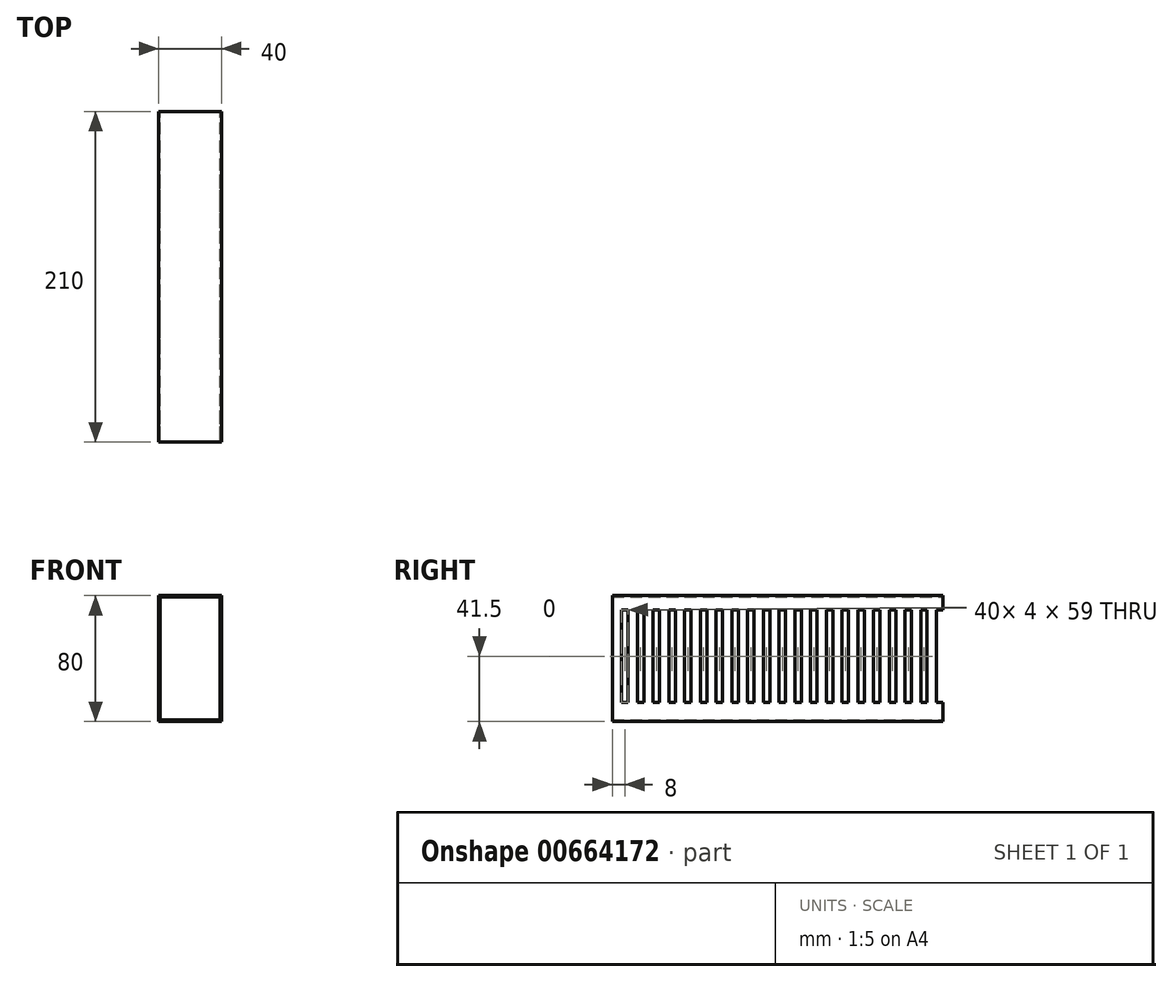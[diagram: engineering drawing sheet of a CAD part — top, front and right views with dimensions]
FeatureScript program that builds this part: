
annotation { "Feature Type Name" : "Feature", "Feature Type Description" : "" }
export const myFeature = defineFeature(function(context is Context, id is Id, definition is map)
    precondition{}
    {
        {
            assignVariable(context, id + "F0", {"name" : "TrunkingLength", "anyValue" : 210});
        }
        {
            var Q0;
            Q0=qCreatedBy(makeId("Front.planeOp"),FACE);
            var sketch = newSketch(context, id + "F1", { "sketchPlane" : qUnion([Q0])});
            skLineSegment(sketch, "E0.bottom", {"start": v(-20, 40) * mm, "end": v(20, 40) * mm});
            skLineSegment(sketch, "E0.top", {"start": v(-20, -40) * mm, "end": v(20, -40) * mm});
            skLineSegment(sketch, "E0.left", {"start": v(-20, 40) * mm, "end": v(-20, -40) * mm});
            skLineSegment(sketch, "E0.right", {"start": v(20, 40) * mm, "end": v(20, -40) * mm});
            skSolve(sketch);
        }
        {
            var Q0;
            Q0=makeQuery(id+"F1.imprint","IMPRINT",FACE,{"disambiguationData":[TD([[makeQuery(id+"F1.imprint","IMPRINT",EDGE,{"derivedFrom":sQuery(id+"F1.wireOp",EDGE,"E0.bottom")}),-1.0]])]});
            extrude(context, id + "F2", {"entities" : qUnion([Q0]), "depth" : (getVariable(context, 'TrunkingLength')) * mm});
        }
        {
            var Q0;
            Q0=makeQuery(id+"F2.opExtrude","CAP_FACE",FACE,{"disambiguationData":[OSD([sQuery(id+"F1.wireOp",EDGE,"E0.bottom"),sQuery(id+"F1.wireOp",EDGE,"E0.top"),sQuery(id+"F1.wireOp",EDGE,"E0.left"),sQuery(id+"F1.wireOp",EDGE,"E0.right")])],"isStart":false});
            var Q1;
            Q1=makeQuery(id+"F2.opExtrude","CAP_FACE",FACE,{"disambiguationData":[OSD([sQuery(id+"F1.wireOp",EDGE,"E0.bottom"),sQuery(id+"F1.wireOp",EDGE,"E0.top"),sQuery(id+"F1.wireOp",EDGE,"E0.left"),sQuery(id+"F1.wireOp",EDGE,"E0.right")])],"isStart":true});
            shell(context, id + "F3", {"entities" : qUnion([Q0, Q1]), "thickness" : 1 * mm});
        }
        {
            var Q0;
            Q0=makeQuery(id+"F2.opExtrude","SWEPT_FACE",FACE,{"disambiguationData":[OSD([sQuery(id+"F1.wireOp",EDGE,"E0.right")])]});
            var sketch = newSketch(context, id + "F4", { "sketchPlane" : qUnion([Q0])});
            skLineSegment(sketch, "E1.bottom", {"start": v(-204, 31) * mm, "end": v(-200, 31) * mm});
            skLineSegment(sketch, "E1.top", {"start": v(-204, -28) * mm, "end": v(-200, -28) * mm});
            skLineSegment(sketch, "E1.left", {"start": v(-204, 31) * mm, "end": v(-204, -28) * mm});
            skLineSegment(sketch, "E1.right", {"start": v(-200, 31) * mm, "end": v(-200, -28) * mm});
            skLineSegment(sketch, "E2.1.0.0", {"start": v(-194, 31) * mm, "end": v(-194, -28) * mm});
            skLineSegment(sketch, "E2.1.0.1", {"start": v(-190, 31) * mm, "end": v(-190, -28) * mm});
            skLineSegment(sketch, "E2.1.0.2", {"start": v(-194, 31) * mm, "end": v(-190, 31) * mm});
            skLineSegment(sketch, "E2.1.0.3", {"start": v(-194, -28) * mm, "end": v(-190, -28) * mm});
            skLineSegment(sketch, "E2.2.0.0", {"start": v(-184, 31) * mm, "end": v(-184, -28) * mm});
            skLineSegment(sketch, "E2.2.0.1", {"start": v(-180, 31) * mm, "end": v(-180, -28) * mm});
            skLineSegment(sketch, "E2.2.0.2", {"start": v(-184, 31) * mm, "end": v(-180, 31) * mm});
            skLineSegment(sketch, "E2.2.0.3", {"start": v(-184, -28) * mm, "end": v(-180, -28) * mm});
            skLineSegment(sketch, "E2.3.0.0", {"start": v(-174, 31) * mm, "end": v(-174, -28) * mm});
            skLineSegment(sketch, "E2.3.0.1", {"start": v(-170, 31) * mm, "end": v(-170, -28) * mm});
            skLineSegment(sketch, "E2.3.0.2", {"start": v(-174, 31) * mm, "end": v(-170, 31) * mm});
            skLineSegment(sketch, "E2.3.0.3", {"start": v(-174, -28) * mm, "end": v(-170, -28) * mm});
            skLineSegment(sketch, "E2.4.0.0", {"start": v(-164, 31) * mm, "end": v(-164, -28) * mm});
            skLineSegment(sketch, "E2.4.0.1", {"start": v(-160, 31) * mm, "end": v(-160, -28) * mm});
            skLineSegment(sketch, "E2.4.0.2", {"start": v(-164, 31) * mm, "end": v(-160, 31) * mm});
            skLineSegment(sketch, "E2.4.0.3", {"start": v(-164, -28) * mm, "end": v(-160, -28) * mm});
            skLineSegment(sketch, "E2.5.0.0", {"start": v(-154, 31) * mm, "end": v(-154, -28) * mm});
            skLineSegment(sketch, "E2.5.0.1", {"start": v(-150, 31) * mm, "end": v(-150, -28) * mm});
            skLineSegment(sketch, "E2.5.0.2", {"start": v(-154, 31) * mm, "end": v(-150, 31) * mm});
            skLineSegment(sketch, "E2.5.0.3", {"start": v(-154, -28) * mm, "end": v(-150, -28) * mm});
            skLineSegment(sketch, "E2.6.0.0", {"start": v(-144, 31) * mm, "end": v(-144, -28) * mm});
            skLineSegment(sketch, "E2.6.0.1", {"start": v(-140, 31) * mm, "end": v(-140, -28) * mm});
            skLineSegment(sketch, "E2.6.0.2", {"start": v(-144, 31) * mm, "end": v(-140, 31) * mm});
            skLineSegment(sketch, "E2.6.0.3", {"start": v(-144, -28) * mm, "end": v(-140, -28) * mm});
            skLineSegment(sketch, "E2.7.0.0", {"start": v(-134, 31) * mm, "end": v(-134, -28) * mm});
            skLineSegment(sketch, "E2.7.0.1", {"start": v(-130, 31) * mm, "end": v(-130, -28) * mm});
            skLineSegment(sketch, "E2.7.0.2", {"start": v(-134, 31) * mm, "end": v(-130, 31) * mm});
            skLineSegment(sketch, "E2.7.0.3", {"start": v(-134, -28) * mm, "end": v(-130, -28) * mm});
            skLineSegment(sketch, "E2.8.0.0", {"start": v(-124, 31) * mm, "end": v(-124, -28) * mm});
            skLineSegment(sketch, "E2.8.0.1", {"start": v(-120, 31) * mm, "end": v(-120, -28) * mm});
            skLineSegment(sketch, "E2.8.0.2", {"start": v(-124, 31) * mm, "end": v(-120, 31) * mm});
            skLineSegment(sketch, "E2.8.0.3", {"start": v(-124, -28) * mm, "end": v(-120, -28) * mm});
            skLineSegment(sketch, "E2.9.0.0", {"start": v(-114, 31) * mm, "end": v(-114, -28) * mm});
            skLineSegment(sketch, "E2.9.0.1", {"start": v(-110, 31) * mm, "end": v(-110, -28) * mm});
            skLineSegment(sketch, "E2.9.0.2", {"start": v(-114, 31) * mm, "end": v(-110, 31) * mm});
            skLineSegment(sketch, "E2.9.0.3", {"start": v(-114, -28) * mm, "end": v(-110, -28) * mm});
            skLineSegment(sketch, "E2.10.0.0", {"start": v(-104, 31) * mm, "end": v(-104, -28) * mm});
            skLineSegment(sketch, "E2.10.0.1", {"start": v(-100, 31) * mm, "end": v(-100, -28) * mm});
            skLineSegment(sketch, "E2.10.0.2", {"start": v(-104, 31) * mm, "end": v(-100, 31) * mm});
            skLineSegment(sketch, "E2.10.0.3", {"start": v(-104, -28) * mm, "end": v(-100, -28) * mm});
            skLineSegment(sketch, "E2.11.0.0", {"start": v(-94, 31) * mm, "end": v(-94, -28) * mm});
            skLineSegment(sketch, "E2.11.0.1", {"start": v(-90, 31) * mm, "end": v(-90, -28) * mm});
            skLineSegment(sketch, "E2.11.0.2", {"start": v(-94, 31) * mm, "end": v(-90, 31) * mm});
            skLineSegment(sketch, "E2.11.0.3", {"start": v(-94, -28) * mm, "end": v(-90, -28) * mm});
            skLineSegment(sketch, "E2.12.0.0", {"start": v(-84, 31) * mm, "end": v(-84, -28) * mm});
            skLineSegment(sketch, "E2.12.0.1", {"start": v(-80, 31) * mm, "end": v(-80, -28) * mm});
            skLineSegment(sketch, "E2.12.0.2", {"start": v(-84, 31) * mm, "end": v(-80, 31) * mm});
            skLineSegment(sketch, "E2.12.0.3", {"start": v(-84, -28) * mm, "end": v(-80, -28) * mm});
            skLineSegment(sketch, "E2.13.0.0", {"start": v(-74, 31) * mm, "end": v(-74, -28) * mm});
            skLineSegment(sketch, "E2.13.0.1", {"start": v(-70, 31) * mm, "end": v(-70, -28) * mm});
            skLineSegment(sketch, "E2.13.0.2", {"start": v(-74, 31) * mm, "end": v(-70, 31) * mm});
            skLineSegment(sketch, "E2.13.0.3", {"start": v(-74, -28) * mm, "end": v(-70, -28) * mm});
            skLineSegment(sketch, "E2.14.0.0", {"start": v(-64, 31) * mm, "end": v(-64, -28) * mm});
            skLineSegment(sketch, "E2.14.0.1", {"start": v(-60, 31) * mm, "end": v(-60, -28) * mm});
            skLineSegment(sketch, "E2.14.0.2", {"start": v(-64, 31) * mm, "end": v(-60, 31) * mm});
            skLineSegment(sketch, "E2.14.0.3", {"start": v(-64, -28) * mm, "end": v(-60, -28) * mm});
            skLineSegment(sketch, "E2.15.0.0", {"start": v(-54, 31) * mm, "end": v(-54, -28) * mm});
            skLineSegment(sketch, "E2.15.0.1", {"start": v(-50, 31) * mm, "end": v(-50, -28) * mm});
            skLineSegment(sketch, "E2.15.0.2", {"start": v(-54, 31) * mm, "end": v(-50, 31) * mm});
            skLineSegment(sketch, "E2.15.0.3", {"start": v(-54, -28) * mm, "end": v(-50, -28) * mm});
            skLineSegment(sketch, "E2.16.0.0", {"start": v(-44, 31) * mm, "end": v(-44, -28) * mm});
            skLineSegment(sketch, "E2.16.0.1", {"start": v(-40, 31) * mm, "end": v(-40, -28) * mm});
            skLineSegment(sketch, "E2.16.0.2", {"start": v(-44, 31) * mm, "end": v(-40, 31) * mm});
            skLineSegment(sketch, "E2.16.0.3", {"start": v(-44, -28) * mm, "end": v(-40, -28) * mm});
            skLineSegment(sketch, "E2.17.0.0", {"start": v(-34, 31) * mm, "end": v(-34, -28) * mm});
            skLineSegment(sketch, "E2.17.0.1", {"start": v(-30, 31) * mm, "end": v(-30, -28) * mm});
            skLineSegment(sketch, "E2.17.0.2", {"start": v(-34, 31) * mm, "end": v(-30, 31) * mm});
            skLineSegment(sketch, "E2.17.0.3", {"start": v(-34, -28) * mm, "end": v(-30, -28) * mm});
            skLineSegment(sketch, "E2.18.0.0", {"start": v(-24, 31) * mm, "end": v(-24, -28) * mm});
            skLineSegment(sketch, "E2.18.0.1", {"start": v(-20, 31) * mm, "end": v(-20, -28) * mm});
            skLineSegment(sketch, "E2.18.0.2", {"start": v(-24, 31) * mm, "end": v(-20, 31) * mm});
            skLineSegment(sketch, "E2.18.0.3", {"start": v(-24, -28) * mm, "end": v(-20, -28) * mm});
            skLineSegment(sketch, "E2.19.0.0", {"start": v(-14, 31) * mm, "end": v(-14, -28) * mm});
            skLineSegment(sketch, "E2.19.0.1", {"start": v(-10, 31) * mm, "end": v(-10, -28) * mm});
            skLineSegment(sketch, "E2.19.0.2", {"start": v(-14, 31) * mm, "end": v(-10, 31) * mm});
            skLineSegment(sketch, "E2.19.0.3", {"start": v(-14, -28) * mm, "end": v(-10, -28) * mm});
            skLineSegment(sketch, "E2.20.0.0", {"start": v(-4, 31) * mm, "end": v(-4, -28) * mm});
            skLineSegment(sketch, "E2.20.0.1", {"start": v(0, 31) * mm, "end": v(0, -28) * mm});
            skLineSegment(sketch, "E2.20.0.2", {"start": v(-4, 31) * mm, "end": v(0, 31) * mm});
            skLineSegment(sketch, "E2.20.0.3", {"start": v(-4, -28) * mm, "end": v(0, -28) * mm});
            skLineSegment(sketch, "E2.21.0.0", {"start": v(6, 31) * mm, "end": v(6, -28) * mm});
            skLineSegment(sketch, "E2.21.0.1", {"start": v(10, 31) * mm, "end": v(10, -28) * mm});
            skLineSegment(sketch, "E2.21.0.2", {"start": v(6, 31) * mm, "end": v(10, 31) * mm});
            skLineSegment(sketch, "E2.21.0.3", {"start": v(6, -28) * mm, "end": v(10, -28) * mm});
            skLineSegment(sketch, "E2.22.0.0", {"start": v(16, 31) * mm, "end": v(16, -28) * mm});
            skLineSegment(sketch, "E2.22.0.1", {"start": v(20, 31) * mm, "end": v(20, -28) * mm});
            skLineSegment(sketch, "E2.22.0.2", {"start": v(16, 31) * mm, "end": v(20, 31) * mm});
            skLineSegment(sketch, "E2.22.0.3", {"start": v(16, -28) * mm, "end": v(20, -28) * mm});
            skLineSegment(sketch, "E2.23.0.0", {"start": v(26, 31) * mm, "end": v(26, -28) * mm});
            skLineSegment(sketch, "E2.23.0.1", {"start": v(30, 31) * mm, "end": v(30, -28) * mm});
            skLineSegment(sketch, "E2.23.0.2", {"start": v(26, 31) * mm, "end": v(30, 31) * mm});
            skLineSegment(sketch, "E2.23.0.3", {"start": v(26, -28) * mm, "end": v(30, -28) * mm});
            skLineSegment(sketch, "E2.24.0.0", {"start": v(36, 31) * mm, "end": v(36, -28) * mm});
            skLineSegment(sketch, "E2.24.0.1", {"start": v(40, 31) * mm, "end": v(40, -28) * mm});
            skLineSegment(sketch, "E2.24.0.2", {"start": v(36, 31) * mm, "end": v(40, 31) * mm});
            skLineSegment(sketch, "E2.24.0.3", {"start": v(36, -28) * mm, "end": v(40, -28) * mm});
            skLineSegment(sketch, "E2.25.0.0", {"start": v(46, 31) * mm, "end": v(46, -28) * mm});
            skLineSegment(sketch, "E2.25.0.1", {"start": v(50, 31) * mm, "end": v(50, -28) * mm});
            skLineSegment(sketch, "E2.25.0.2", {"start": v(46, 31) * mm, "end": v(50, 31) * mm});
            skLineSegment(sketch, "E2.25.0.3", {"start": v(46, -28) * mm, "end": v(50, -28) * mm});
            skLineSegment(sketch, "E2.26.0.0", {"start": v(56, 31) * mm, "end": v(56, -28) * mm});
            skLineSegment(sketch, "E2.26.0.1", {"start": v(60, 31) * mm, "end": v(60, -28) * mm});
            skLineSegment(sketch, "E2.26.0.2", {"start": v(56, 31) * mm, "end": v(60, 31) * mm});
            skLineSegment(sketch, "E2.26.0.3", {"start": v(56, -28) * mm, "end": v(60, -28) * mm});
            skLineSegment(sketch, "E2.27.0.0", {"start": v(66, 31) * mm, "end": v(66, -28) * mm});
            skLineSegment(sketch, "E2.27.0.1", {"start": v(70, 31) * mm, "end": v(70, -28) * mm});
            skLineSegment(sketch, "E2.27.0.2", {"start": v(66, 31) * mm, "end": v(70, 31) * mm});
            skLineSegment(sketch, "E2.27.0.3", {"start": v(66, -28) * mm, "end": v(70, -28) * mm});
            skLineSegment(sketch, "E2.28.0.0", {"start": v(76, 31) * mm, "end": v(76, -28) * mm});
            skLineSegment(sketch, "E2.28.0.1", {"start": v(80, 31) * mm, "end": v(80, -28) * mm});
            skLineSegment(sketch, "E2.28.0.2", {"start": v(76, 31) * mm, "end": v(80, 31) * mm});
            skLineSegment(sketch, "E2.28.0.3", {"start": v(76, -28) * mm, "end": v(80, -28) * mm});
            skLineSegment(sketch, "E2.29.0.0", {"start": v(86, 31) * mm, "end": v(86, -28) * mm});
            skLineSegment(sketch, "E2.29.0.1", {"start": v(90, 31) * mm, "end": v(90, -28) * mm});
            skLineSegment(sketch, "E2.29.0.2", {"start": v(86, 31) * mm, "end": v(90, 31) * mm});
            skLineSegment(sketch, "E2.29.0.3", {"start": v(86, -28) * mm, "end": v(90, -28) * mm});
            skLineSegment(sketch, "E2.30.0.0", {"start": v(96, 31) * mm, "end": v(96, -28) * mm});
            skLineSegment(sketch, "E2.30.0.1", {"start": v(100, 31) * mm, "end": v(100, -28) * mm});
            skLineSegment(sketch, "E2.30.0.2", {"start": v(96, 31) * mm, "end": v(100, 31) * mm});
            skLineSegment(sketch, "E2.30.0.3", {"start": v(96, -28) * mm, "end": v(100, -28) * mm});
            skLineSegment(sketch, "E2.31.0.0", {"start": v(106, 31) * mm, "end": v(106, -28) * mm});
            skLineSegment(sketch, "E2.31.0.1", {"start": v(110, 31) * mm, "end": v(110, -28) * mm});
            skLineSegment(sketch, "E2.31.0.2", {"start": v(106, 31) * mm, "end": v(110, 31) * mm});
            skLineSegment(sketch, "E2.31.0.3", {"start": v(106, -28) * mm, "end": v(110, -28) * mm});
            skLineSegment(sketch, "E2.32.0.0", {"start": v(116, 31) * mm, "end": v(116, -28) * mm});
            skLineSegment(sketch, "E2.32.0.1", {"start": v(120, 31) * mm, "end": v(120, -28) * mm});
            skLineSegment(sketch, "E2.32.0.2", {"start": v(116, 31) * mm, "end": v(120, 31) * mm});
            skLineSegment(sketch, "E2.32.0.3", {"start": v(116, -28) * mm, "end": v(120, -28) * mm});
            skLineSegment(sketch, "E2.33.0.0", {"start": v(126, 31) * mm, "end": v(126, -28) * mm});
            skLineSegment(sketch, "E2.33.0.1", {"start": v(130, 31) * mm, "end": v(130, -28) * mm});
            skLineSegment(sketch, "E2.33.0.2", {"start": v(126, 31) * mm, "end": v(130, 31) * mm});
            skLineSegment(sketch, "E2.33.0.3", {"start": v(126, -28) * mm, "end": v(130, -28) * mm});
            skLineSegment(sketch, "E2.34.0.0", {"start": v(136, 31) * mm, "end": v(136, -28) * mm});
            skLineSegment(sketch, "E2.34.0.1", {"start": v(140, 31) * mm, "end": v(140, -28) * mm});
            skLineSegment(sketch, "E2.34.0.2", {"start": v(136, 31) * mm, "end": v(140, 31) * mm});
            skLineSegment(sketch, "E2.34.0.3", {"start": v(136, -28) * mm, "end": v(140, -28) * mm});
            skLineSegment(sketch, "E2.35.0.0", {"start": v(146, 31) * mm, "end": v(146, -28) * mm});
            skLineSegment(sketch, "E2.35.0.1", {"start": v(150, 31) * mm, "end": v(150, -28) * mm});
            skLineSegment(sketch, "E2.35.0.2", {"start": v(146, 31) * mm, "end": v(150, 31) * mm});
            skLineSegment(sketch, "E2.35.0.3", {"start": v(146, -28) * mm, "end": v(150, -28) * mm});
            skLineSegment(sketch, "E2.36.0.0", {"start": v(156, 31) * mm, "end": v(156, -28) * mm});
            skLineSegment(sketch, "E2.36.0.1", {"start": v(160, 31) * mm, "end": v(160, -28) * mm});
            skLineSegment(sketch, "E2.36.0.2", {"start": v(156, 31) * mm, "end": v(160, 31) * mm});
            skLineSegment(sketch, "E2.36.0.3", {"start": v(156, -28) * mm, "end": v(160, -28) * mm});
            skLineSegment(sketch, "E2.37.0.0", {"start": v(166, 31) * mm, "end": v(166, -28) * mm});
            skLineSegment(sketch, "E2.37.0.1", {"start": v(170, 31) * mm, "end": v(170, -28) * mm});
            skLineSegment(sketch, "E2.37.0.2", {"start": v(166, 31) * mm, "end": v(170, 31) * mm});
            skLineSegment(sketch, "E2.37.0.3", {"start": v(166, -28) * mm, "end": v(170, -28) * mm});
            skLineSegment(sketch, "E2.38.0.0", {"start": v(176, 31) * mm, "end": v(176, -28) * mm});
            skLineSegment(sketch, "E2.38.0.1", {"start": v(180, 31) * mm, "end": v(180, -28) * mm});
            skLineSegment(sketch, "E2.38.0.2", {"start": v(176, 31) * mm, "end": v(180, 31) * mm});
            skLineSegment(sketch, "E2.38.0.3", {"start": v(176, -28) * mm, "end": v(180, -28) * mm});
            skLineSegment(sketch, "E2.39.0.0", {"start": v(186, 31) * mm, "end": v(186, -28) * mm});
            skLineSegment(sketch, "E2.39.0.1", {"start": v(190, 31) * mm, "end": v(190, -28) * mm});
            skLineSegment(sketch, "E2.39.0.2", {"start": v(186, 31) * mm, "end": v(190, 31) * mm});
            skLineSegment(sketch, "E2.39.0.3", {"start": v(186, -28) * mm, "end": v(190, -28) * mm});
            skLineSegment(sketch, "E2.40.0.0", {"start": v(196, 31) * mm, "end": v(196, -28) * mm});
            skLineSegment(sketch, "E2.40.0.1", {"start": v(200, 31) * mm, "end": v(200, -28) * mm});
            skLineSegment(sketch, "E2.40.0.2", {"start": v(196, 31) * mm, "end": v(200, 31) * mm});
            skLineSegment(sketch, "E2.40.0.3", {"start": v(196, -28) * mm, "end": v(200, -28) * mm});
            skLineSegment(sketch, "E2.41.0.0", {"start": v(206, 31) * mm, "end": v(206, -28) * mm});
            skLineSegment(sketch, "E2.41.0.1", {"start": v(210, 31) * mm, "end": v(210, -28) * mm});
            skLineSegment(sketch, "E2.41.0.2", {"start": v(206, 31) * mm, "end": v(210, 31) * mm});
            skLineSegment(sketch, "E2.41.0.3", {"start": v(206, -28) * mm, "end": v(210, -28) * mm});
            skLineSegment(sketch, "E2.42.0.0", {"start": v(216, 31) * mm, "end": v(216, -28) * mm});
            skLineSegment(sketch, "E2.42.0.1", {"start": v(220, 31) * mm, "end": v(220, -28) * mm});
            skLineSegment(sketch, "E2.42.0.2", {"start": v(216, 31) * mm, "end": v(220, 31) * mm});
            skLineSegment(sketch, "E2.42.0.3", {"start": v(216, -28) * mm, "end": v(220, -28) * mm});
            skLineSegment(sketch, "E2.43.0.0", {"start": v(226, 31) * mm, "end": v(226, -28) * mm});
            skLineSegment(sketch, "E2.43.0.1", {"start": v(230, 31) * mm, "end": v(230, -28) * mm});
            skLineSegment(sketch, "E2.43.0.2", {"start": v(226, 31) * mm, "end": v(230, 31) * mm});
            skLineSegment(sketch, "E2.43.0.3", {"start": v(226, -28) * mm, "end": v(230, -28) * mm});
            skLineSegment(sketch, "E2.44.0.0", {"start": v(236, 31) * mm, "end": v(236, -28) * mm});
            skLineSegment(sketch, "E2.44.0.1", {"start": v(240, 31) * mm, "end": v(240, -28) * mm});
            skLineSegment(sketch, "E2.44.0.2", {"start": v(236, 31) * mm, "end": v(240, 31) * mm});
            skLineSegment(sketch, "E2.44.0.3", {"start": v(236, -28) * mm, "end": v(240, -28) * mm});
            skLineSegment(sketch, "E2.direction1", {"start": v(-204, -28) * mm, "end": v(-194, -28) * mm, "construction": true});
            skSolve(sketch);
        }
        {
            var Q0;
            Q0=makeQuery(id+"F4.imprint","IMPRINT",FACE,{"disambiguationData":[TD([[makeQuery(id+"F4.imprint","IMPRINT",EDGE,{"derivedFrom":sQuery(id+"F4.wireOp",EDGE,"E1.bottom")}),-1.0]])]});
            var Q1;
            Q1=makeQuery(id+"F4.imprint","IMPRINT",FACE,{"disambiguationData":[TD([[makeQuery(id+"F4.imprint","IMPRINT",EDGE,{"derivedFrom":sQuery(id+"F4.wireOp",EDGE,"E2.1.0.0")}),1.0]])]});
            var Q2;
            Q2=makeQuery(id+"F4.imprint","IMPRINT",FACE,{"disambiguationData":[TD([[makeQuery(id+"F4.imprint","IMPRINT",EDGE,{"derivedFrom":sQuery(id+"F4.wireOp",EDGE,"E2.2.0.0")}),1.0]])]});
            var Q3;
            Q3=makeQuery(id+"F4.imprint","IMPRINT",FACE,{"disambiguationData":[TD([[makeQuery(id+"F4.imprint","IMPRINT",EDGE,{"derivedFrom":sQuery(id+"F4.wireOp",EDGE,"E2.3.0.0")}),1.0]])]});
            var Q4;
            Q4=makeQuery(id+"F4.imprint","IMPRINT",FACE,{"disambiguationData":[TD([[makeQuery(id+"F4.imprint","IMPRINT",EDGE,{"derivedFrom":sQuery(id+"F4.wireOp",EDGE,"E2.4.0.0")}),1.0]])]});
            var Q5;
            Q5=makeQuery(id+"F4.imprint","IMPRINT",FACE,{"disambiguationData":[TD([[makeQuery(id+"F4.imprint","IMPRINT",EDGE,{"derivedFrom":sQuery(id+"F4.wireOp",EDGE,"E2.5.0.0")}),1.0]])]});
            var Q6;
            Q6=makeQuery(id+"F4.imprint","IMPRINT",FACE,{"disambiguationData":[TD([[makeQuery(id+"F4.imprint","IMPRINT",EDGE,{"derivedFrom":sQuery(id+"F4.wireOp",EDGE,"E2.6.0.0")}),1.0]])]});
            var Q7;
            Q7=makeQuery(id+"F4.imprint","IMPRINT",FACE,{"disambiguationData":[TD([[makeQuery(id+"F4.imprint","IMPRINT",EDGE,{"derivedFrom":sQuery(id+"F4.wireOp",EDGE,"E2.7.0.0")}),1.0]])]});
            var Q8;
            Q8=makeQuery(id+"F4.imprint","IMPRINT",FACE,{"disambiguationData":[TD([[makeQuery(id+"F4.imprint","IMPRINT",EDGE,{"derivedFrom":sQuery(id+"F4.wireOp",EDGE,"E2.8.0.0")}),1.0]])]});
            var Q9;
            Q9=makeQuery(id+"F4.imprint","IMPRINT",FACE,{"disambiguationData":[TD([[makeQuery(id+"F4.imprint","IMPRINT",EDGE,{"derivedFrom":sQuery(id+"F4.wireOp",EDGE,"E2.9.0.0")}),1.0]])]});
            var Q10;
            Q10=makeQuery(id+"F4.imprint","IMPRINT",FACE,{"disambiguationData":[TD([[makeQuery(id+"F4.imprint","IMPRINT",EDGE,{"derivedFrom":sQuery(id+"F4.wireOp",EDGE,"E2.10.0.0")}),1.0]])]});
            var Q11;
            Q11=makeQuery(id+"F4.imprint","IMPRINT",FACE,{"disambiguationData":[TD([[makeQuery(id+"F4.imprint","IMPRINT",EDGE,{"derivedFrom":sQuery(id+"F4.wireOp",EDGE,"E2.11.0.0")}),1.0]])]});
            var Q12;
            Q12=makeQuery(id+"F4.imprint","IMPRINT",FACE,{"disambiguationData":[TD([[makeQuery(id+"F4.imprint","IMPRINT",EDGE,{"derivedFrom":sQuery(id+"F4.wireOp",EDGE,"E2.12.0.0")}),1.0]])]});
            var Q13;
            Q13=makeQuery(id+"F4.imprint","IMPRINT",FACE,{"disambiguationData":[TD([[makeQuery(id+"F4.imprint","IMPRINT",EDGE,{"derivedFrom":sQuery(id+"F4.wireOp",EDGE,"E2.13.0.0")}),1.0]])]});
            var Q14;
            Q14=makeQuery(id+"F4.imprint","IMPRINT",FACE,{"disambiguationData":[TD([[makeQuery(id+"F4.imprint","IMPRINT",EDGE,{"derivedFrom":sQuery(id+"F4.wireOp",EDGE,"E2.14.0.0")}),1.0]])]});
            var Q15;
            Q15=makeQuery(id+"F4.imprint","IMPRINT",FACE,{"disambiguationData":[TD([[makeQuery(id+"F4.imprint","IMPRINT",EDGE,{"derivedFrom":sQuery(id+"F4.wireOp",EDGE,"E2.15.0.0")}),1.0]])]});
            var Q16;
            Q16=makeQuery(id+"F4.imprint","IMPRINT",FACE,{"disambiguationData":[TD([[makeQuery(id+"F4.imprint","IMPRINT",EDGE,{"derivedFrom":sQuery(id+"F4.wireOp",EDGE,"E2.16.0.0")}),1.0]])]});
            var Q17;
            Q17=makeQuery(id+"F4.imprint","IMPRINT",FACE,{"disambiguationData":[TD([[makeQuery(id+"F4.imprint","IMPRINT",EDGE,{"derivedFrom":sQuery(id+"F4.wireOp",EDGE,"E2.17.0.0")}),1.0]])]});
            var Q18;
            Q18=makeQuery(id+"F4.imprint","IMPRINT",FACE,{"disambiguationData":[TD([[makeQuery(id+"F4.imprint","IMPRINT",EDGE,{"derivedFrom":sQuery(id+"F4.wireOp",EDGE,"E2.18.0.0")}),1.0]])]});
            var Q19;
            Q19=makeQuery(id+"F4.imprint","IMPRINT",FACE,{"disambiguationData":[TD([[makeQuery(id+"F4.imprint","IMPRINT",EDGE,{"derivedFrom":sQuery(id+"F4.wireOp",EDGE,"E2.19.0.0")}),1.0]])]});
            var Q20;
            Q20=makeQuery(id+"F4.imprint","IMPRINT",FACE,{"disambiguationData":[TD([[makeQuery(id+"F4.imprint","IMPRINT",EDGE,{"derivedFrom":sQuery(id+"F4.wireOp",EDGE,"E2.20.0.0")}),1.0]])]});
            var Q21;
            Q21=makeQuery(id+"F4.imprint","IMPRINT",FACE,{"disambiguationData":[TD([[makeQuery(id+"F4.imprint","IMPRINT",EDGE,{"derivedFrom":sQuery(id+"F4.wireOp",EDGE,"E2.21.0.0")}),1.0]])]});
            var Q22;
            Q22=makeQuery(id+"F4.imprint","IMPRINT",FACE,{"disambiguationData":[TD([[makeQuery(id+"F4.imprint","IMPRINT",EDGE,{"derivedFrom":sQuery(id+"F4.wireOp",EDGE,"E2.22.0.0")}),1.0]])]});
            var Q23;
            Q23=makeQuery(id+"F4.imprint","IMPRINT",FACE,{"disambiguationData":[TD([[makeQuery(id+"F4.imprint","IMPRINT",EDGE,{"derivedFrom":sQuery(id+"F4.wireOp",EDGE,"E2.23.0.0")}),1.0]])]});
            var Q24;
            Q24=makeQuery(id+"F4.imprint","IMPRINT",FACE,{"disambiguationData":[TD([[makeQuery(id+"F4.imprint","IMPRINT",EDGE,{"derivedFrom":sQuery(id+"F4.wireOp",EDGE,"E2.24.0.0")}),1.0]])]});
            var Q25;
            Q25=makeQuery(id+"F4.imprint","IMPRINT",FACE,{"disambiguationData":[TD([[makeQuery(id+"F4.imprint","IMPRINT",EDGE,{"derivedFrom":sQuery(id+"F4.wireOp",EDGE,"E2.25.0.0")}),1.0]])]});
            var Q26;
            Q26=makeQuery(id+"F4.imprint","IMPRINT",FACE,{"disambiguationData":[TD([[makeQuery(id+"F4.imprint","IMPRINT",EDGE,{"derivedFrom":sQuery(id+"F4.wireOp",EDGE,"E2.26.0.0")}),1.0]])]});
            var Q27;
            Q27=makeQuery(id+"F4.imprint","IMPRINT",FACE,{"disambiguationData":[TD([[makeQuery(id+"F4.imprint","IMPRINT",EDGE,{"derivedFrom":sQuery(id+"F4.wireOp",EDGE,"E2.27.0.0")}),1.0]])]});
            var Q28;
            Q28=makeQuery(id+"F4.imprint","IMPRINT",FACE,{"disambiguationData":[TD([[makeQuery(id+"F4.imprint","IMPRINT",EDGE,{"derivedFrom":sQuery(id+"F4.wireOp",EDGE,"E2.28.0.0")}),1.0]])]});
            var Q29;
            Q29=makeQuery(id+"F4.imprint","IMPRINT",FACE,{"disambiguationData":[TD([[makeQuery(id+"F4.imprint","IMPRINT",EDGE,{"derivedFrom":sQuery(id+"F4.wireOp",EDGE,"E2.29.0.0")}),1.0]])]});
            var Q30;
            Q30=makeQuery(id+"F4.imprint","IMPRINT",FACE,{"disambiguationData":[TD([[makeQuery(id+"F4.imprint","IMPRINT",EDGE,{"derivedFrom":sQuery(id+"F4.wireOp",EDGE,"E2.30.0.0")}),1.0]])]});
            var Q31;
            Q31=makeQuery(id+"F4.imprint","IMPRINT",FACE,{"disambiguationData":[TD([[makeQuery(id+"F4.imprint","IMPRINT",EDGE,{"derivedFrom":sQuery(id+"F4.wireOp",EDGE,"E2.31.0.0")}),1.0]])]});
            var Q32;
            Q32=makeQuery(id+"F4.imprint","IMPRINT",FACE,{"disambiguationData":[TD([[makeQuery(id+"F4.imprint","IMPRINT",EDGE,{"derivedFrom":sQuery(id+"F4.wireOp",EDGE,"E2.32.0.0")}),1.0]])]});
            var Q33;
            Q33=makeQuery(id+"F4.imprint","IMPRINT",FACE,{"disambiguationData":[TD([[makeQuery(id+"F4.imprint","IMPRINT",EDGE,{"derivedFrom":sQuery(id+"F4.wireOp",EDGE,"E2.33.0.0")}),1.0]])]});
            var Q34;
            Q34=makeQuery(id+"F4.imprint","IMPRINT",FACE,{"disambiguationData":[TD([[makeQuery(id+"F4.imprint","IMPRINT",EDGE,{"derivedFrom":sQuery(id+"F4.wireOp",EDGE,"E2.34.0.0")}),1.0]])]});
            var Q35;
            Q35=makeQuery(id+"F4.imprint","IMPRINT",FACE,{"disambiguationData":[TD([[makeQuery(id+"F4.imprint","IMPRINT",EDGE,{"derivedFrom":sQuery(id+"F4.wireOp",EDGE,"E2.35.0.0")}),1.0]])]});
            var Q36;
            Q36=makeQuery(id+"F4.imprint","IMPRINT",FACE,{"disambiguationData":[TD([[makeQuery(id+"F4.imprint","IMPRINT",EDGE,{"derivedFrom":sQuery(id+"F4.wireOp",EDGE,"E2.36.0.0")}),1.0]])]});
            var Q37;
            Q37=makeQuery(id+"F4.imprint","IMPRINT",FACE,{"disambiguationData":[TD([[makeQuery(id+"F4.imprint","IMPRINT",EDGE,{"derivedFrom":sQuery(id+"F4.wireOp",EDGE,"E2.37.0.0")}),1.0]])]});
            var Q38;
            Q38=makeQuery(id+"F4.imprint","IMPRINT",FACE,{"disambiguationData":[TD([[makeQuery(id+"F4.imprint","IMPRINT",EDGE,{"derivedFrom":sQuery(id+"F4.wireOp",EDGE,"E2.38.0.0")}),1.0]])]});
            var Q39;
            Q39=makeQuery(id+"F4.imprint","IMPRINT",FACE,{"disambiguationData":[TD([[makeQuery(id+"F4.imprint","IMPRINT",EDGE,{"derivedFrom":sQuery(id+"F4.wireOp",EDGE,"E2.40.0.0")}),1.0]])]});
            var Q40;
            Q40=makeQuery(id+"F4.imprint","IMPRINT",FACE,{"disambiguationData":[TD([[makeQuery(id+"F4.imprint","IMPRINT",EDGE,{"derivedFrom":sQuery(id+"F4.wireOp",EDGE,"E2.41.0.0")}),1.0]])]});
            var Q41;
            Q41=makeQuery(id+"F4.imprint","IMPRINT",FACE,{"disambiguationData":[TD([[makeQuery(id+"F4.imprint","IMPRINT",EDGE,{"derivedFrom":sQuery(id+"F4.wireOp",EDGE,"E2.42.0.0")}),1.0]])]});
            var Q42;
            Q42=makeQuery(id+"F4.imprint","IMPRINT",FACE,{"disambiguationData":[TD([[makeQuery(id+"F4.imprint","IMPRINT",EDGE,{"derivedFrom":sQuery(id+"F4.wireOp",EDGE,"E2.43.0.0")}),1.0]])]});
            var Q43;
            Q43=makeQuery(id+"F4.imprint","IMPRINT",FACE,{"disambiguationData":[TD([[makeQuery(id+"F4.imprint","IMPRINT",EDGE,{"derivedFrom":sQuery(id+"F4.wireOp",EDGE,"E2.44.0.0")}),1.0]])]});
            var Q44;
            Q44=makeQuery(id+"F4.imprint","IMPRINT",FACE,{"disambiguationData":[TD([[makeQuery(id+"F4.imprint","IMPRINT",EDGE,{"derivedFrom":sQuery(id+"F4.wireOp",EDGE,"E2.39.0.0")}),1.0]])]});
            extrude(context, id + "F5", {"entities" : qUnion([Q0, Q1, Q2, Q3, Q4, Q5, Q6, Q7, Q8, Q9, Q10, Q11, Q12, Q13, Q14, Q15, Q16, Q17, Q18, Q19, Q20, Q21, Q22, Q23, Q24, Q25, Q26, Q27, Q28, Q29, Q30, Q31, Q32, Q33, Q34, Q35, Q36, Q37, Q38, Q39, Q40, Q41, Q42, Q43, Q44]), "operationType" : NewBodyOperationType.REMOVE, "endBound" : BoundingType.THROUGH_ALL, "oppositeDirection" : true, "depth" : 25 * mm});
        }
    });
